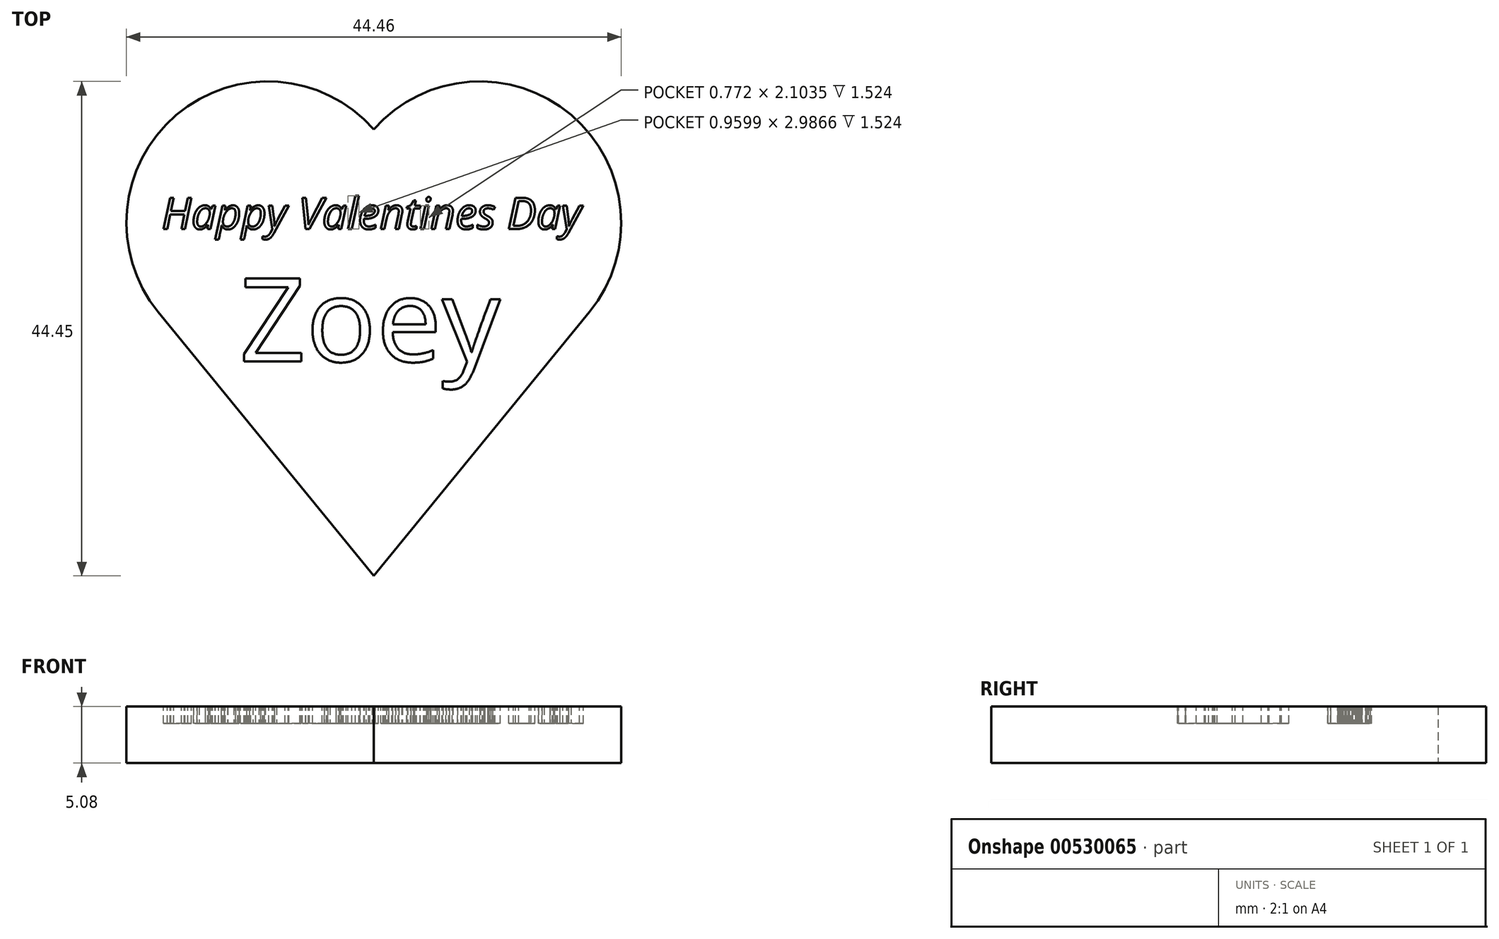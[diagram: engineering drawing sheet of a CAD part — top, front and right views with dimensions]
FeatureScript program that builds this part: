
annotation { "Feature Type Name" : "Feature", "Feature Type Description" : "" }
export const myFeature = defineFeature(function(context is Context, id is Id, definition is map)
    precondition{}
    {
        {
            var Q0;
            Q0=qCreatedBy(makeId("Top.planeOp"),FACE);
            var sketch = newSketch(context, id + "F0", { "sketchPlane" : qUnion([Q0])});
            skArc(sketch, "E0", {"start": v(0, 13.01) * mm, "mid": v(-17.74, 14.3) * mm, "end": v(-19.36, -3.42) * mm});
            skLineSegment(sketch, "E1", {"start": v(0, 24.39) * mm, "end": v(0, -27.14) * mm, "construction": true});
            skArc(sketch, "E2.MirrorC", {"start": v(0, 13.01) * mm, "mid": v(17.74, 14.3) * mm, "end": v(19.36, -3.42) * mm});
            skLineSegment(sketch, "E3", {"start": v(-19.36, -3.42) * mm, "end": v(0, -27.14) * mm});
            skLineSegment(sketch, "E4.MirrorCS", {"start": v(19.36, -3.42) * mm, "end": v(0, -27.14) * mm});
            skSolve(sketch);
        }
        {
            var Q0;
            Q0=makeQuery(id+"F0.imprint","IMPRINT",FACE,{"disambiguationData":[TD([[makeQuery(id+"F0.imprint","IMPRINT",EDGE,{"derivedFrom":sQuery(id+"F0.wireOp",EDGE,"E0")}),1.0]])]});
            extrude(context, id + "F1", {"entities" : qUnion([Q0]), "depth" : 5.08 * mm, "offsetDistance" : 25.4 * mm});
        }
        {
            var Q0;
            Q0=makeQuery(id+"F1.opExtrude","CAP_FACE",FACE,{"disambiguationData":[OSD([sQuery(id+"F0.wireOp",EDGE,"E0"),sQuery(id+"F0.wireOp",EDGE,"E2.MirrorC"),sQuery(id+"F0.wireOp",EDGE,"E3"),sQuery(id+"F0.wireOp",EDGE,"E4.MirrorCS")])],"isStart":false});
            var sketch = newSketch(context, id + "F2", { "sketchPlane" : qUnion([Q0])});
            skText(sketch, "E5", { "text": "Happy Valentines Day", "fontName": "OpenSans-Italic.ttf"});
            skLineSegment(sketch, "E6", {"start": v(0, 0) * mm, "end": v(0, 7.06) * mm, "construction": true});
            skText(sketch, "E7", { "text": "Zoey", "fontName": "OpenSans-Regular.ttf"});
            const initialGuessF2  = {"E5": [-0.01905, 0.00404, 1, 0, 0.00283], "E7": [-0.01207, -0.00787, 1, 0, 0.00754]};
            skSetInitialGuess(sketch, initialGuessF2);
            skSolve(sketch);
        }
        {
            var Q0;
            Q0 = qSketchRegion(id + "F2", true);
            extrude(context, id + "F3", {"entities" : qUnion([Q0]), "operationType" : NewBodyOperationType.REMOVE, "oppositeDirection" : true, "depth" : 1.52 * mm, "offsetDistance" : 25.4 * mm});
        }
    });
